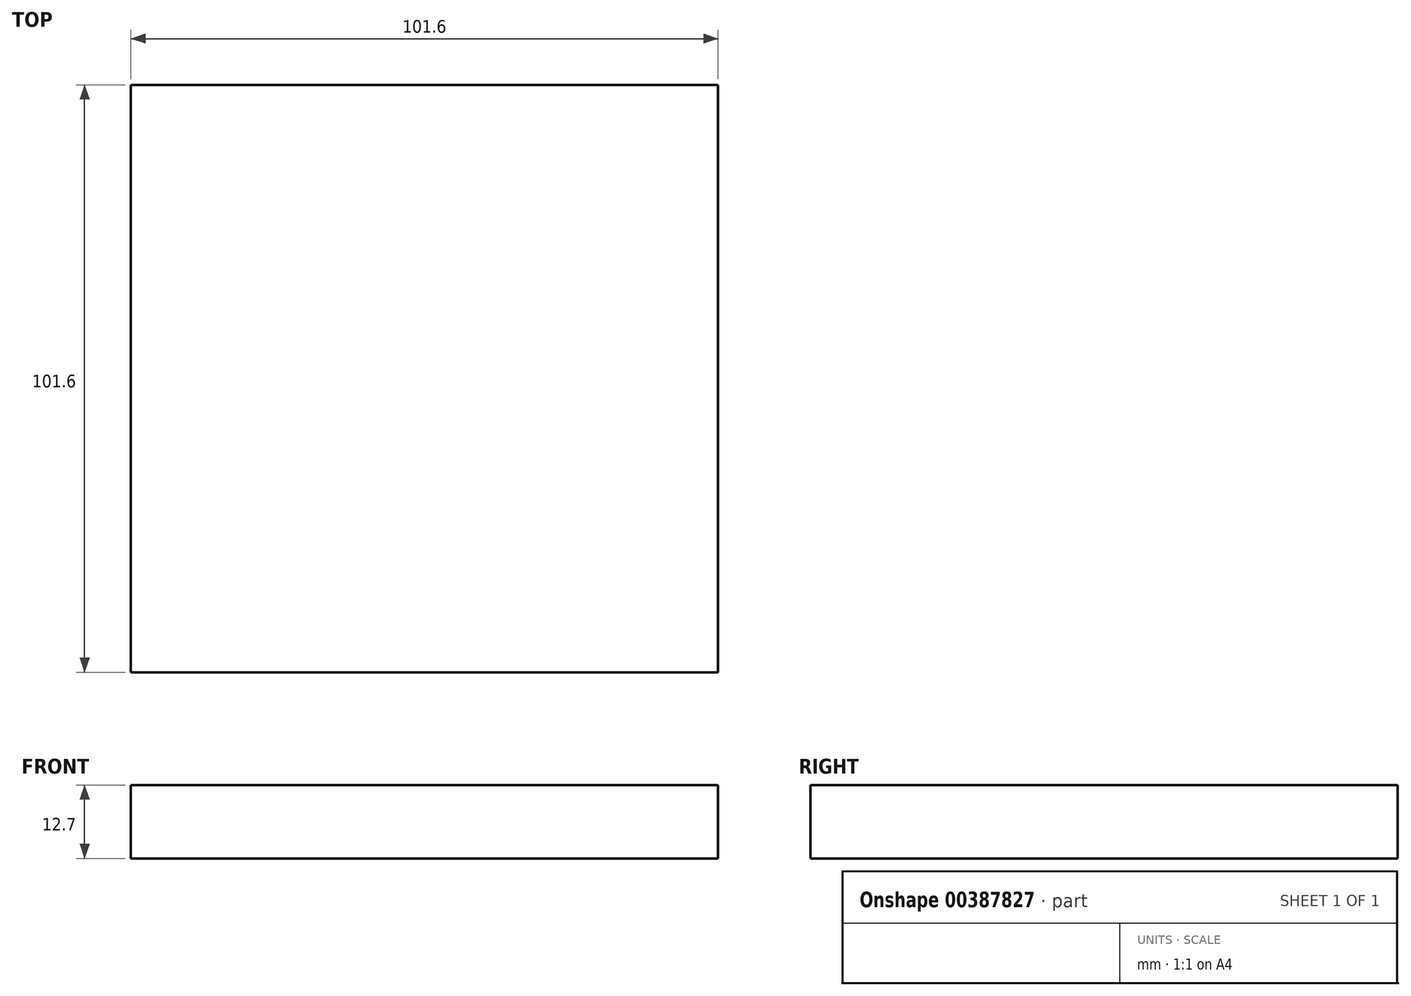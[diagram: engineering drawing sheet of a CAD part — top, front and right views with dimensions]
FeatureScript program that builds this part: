
annotation { "Feature Type Name" : "Feature", "Feature Type Description" : "" }
export const myFeature = defineFeature(function(context is Context, id is Id, definition is map)
    precondition{}
    {
        {
            var Q0;
            Q0=qCreatedBy(makeId("Top.planeOp"),FACE);
            var sketch = newSketch(context, id + "F0", { "sketchPlane" : qUnion([Q0])});
            skLineSegment(sketch, "E0.bottom", {"start": v(-50.8, -50.8) * mm, "end": v(50.8, -50.8) * mm});
            skLineSegment(sketch, "E0.top", {"start": v(-50.8, 50.8) * mm, "end": v(50.8, 50.8) * mm});
            skLineSegment(sketch, "E0.left", {"start": v(-50.8, -50.8) * mm, "end": v(-50.8, 50.8) * mm});
            skLineSegment(sketch, "E0.right", {"start": v(50.8, -50.8) * mm, "end": v(50.8, 50.8) * mm});
            skSolve(sketch);
        }
        {
            var Q0;
            Q0 = qSketchRegion(id + "F0", true);
            extrude(context, id + "F1", {"entities" : qUnion([Q0]), "depth" : 12.7 * mm});
        }
    });
